# Revit family: UM371LP Banco Ela Plus
name_source: partatom
category: Mobiliario
units: mm (PartAtom-declared; Revit-internal decimal feet)

## family parameters
Compartido = No
Corte con vacíos al cargar = No
Número OmniClass = 23.40.20.00
Punto de cálculo de habitación = No
Se basa en plano de trabajo = No
Siempre vertical = Sí
Título OmniClass = General Furniture and Specialties

## types (1)
- UM371LP Banco Ela Plus
    Acabado Listones = Lignus, protector fungicida, insecticida e hidrófugo.
    Acabado bancada = Color blanco granítico pulido.
    Accessibilidad = Sí
    Altura asiento = 460 mm  [stored 1.50919 ft]
    Altura total = 870 mm  [stored 2.85433 ft]
    Ancho = 800 mm  [stored 2.62467 ft]
    Comentarios de tipo = Asiento de hormigón armado hidrófugo moldeado, color blanco granítico pulido. Estructura de acero inoxidable mate. Opcional se puede combinar con listones de madera tropical de sección 110x35mm,
tradata con Lignus , protector fungicida, insecticida e hidrófugo. Acabado color natural.
    Fabricante = BENITO
    Ficha tecnica = http://www.benito.com
    Instalación = Apoyado por su propio peso.
    Largo = 3000 mm  [stored 9.84252 ft]
    Material bancada = Hormigón armado hidrófugo.
    Material listones = Madera Tropical
    Modelo = Banco Ela Plus
    Referencia = UM371LP
    URL = http://www.benito.com
    URL Producto = http://www.benito.com

note: [stored X ft] marks values corroborated as IEEE doubles in the binary element streams (Revit-internal decimal feet)

## geometry (parser evidence)
native form markers: Blend x4
no freeform markers — native parametric forms only
